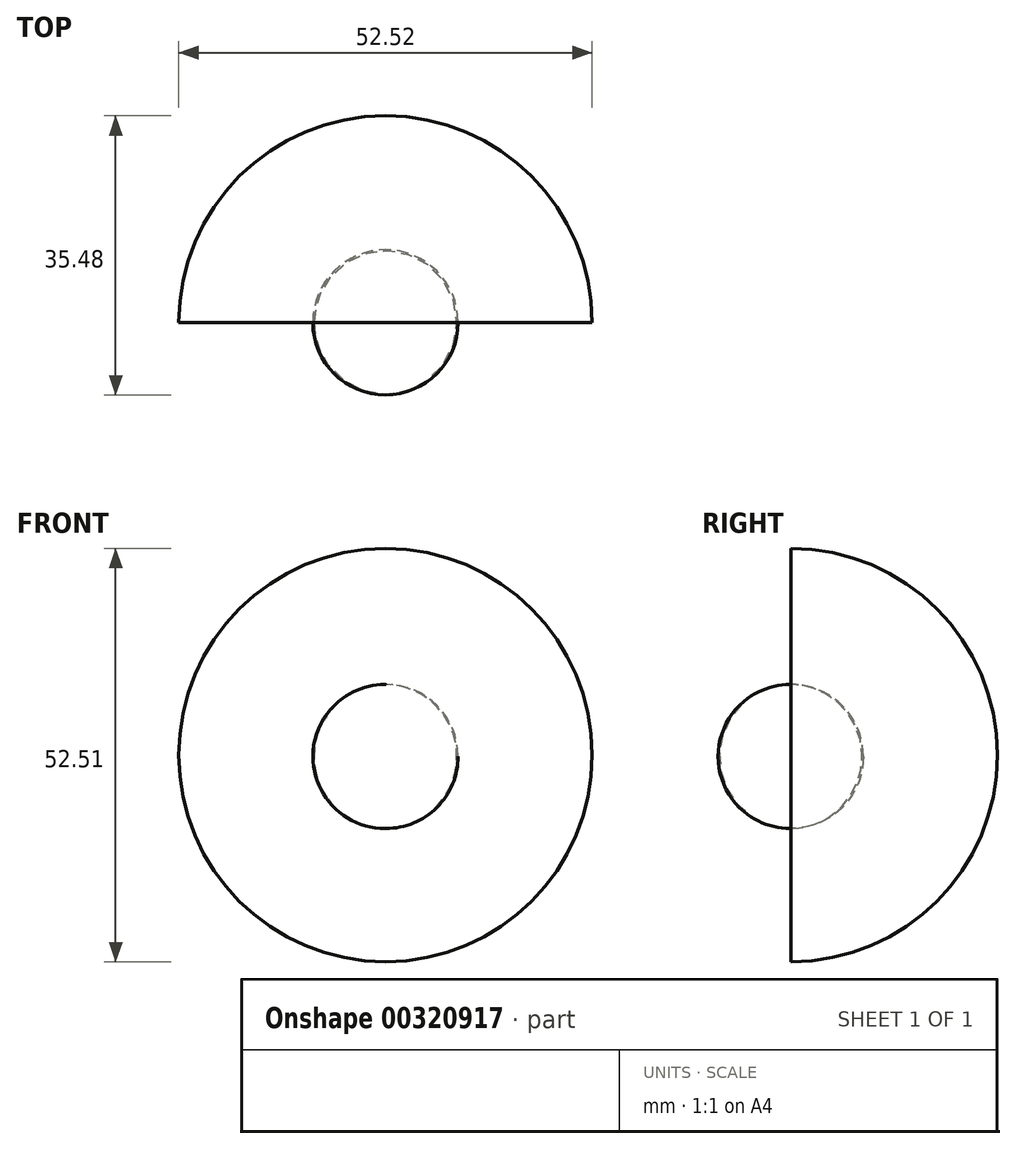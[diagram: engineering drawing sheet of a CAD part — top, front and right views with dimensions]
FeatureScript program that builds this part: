
annotation { "Feature Type Name" : "Feature", "Feature Type Description" : "" }
export const myFeature = defineFeature(function(context is Context, id is Id, definition is map)
    precondition{}
    {
        {
            var Q0;
            Q0=qCreatedBy(makeId("Front.planeOp"),FACE);
            var sketch = newSketch(context, id + "F0", { "sketchPlane" : qUnion([Q0])});
            skLineSegment(sketch, "E0", {"start": v(0, 0) * mm, "end": v(0, 52.51) * mm});
            skArc(sketch, "E1", {"start": v(0, 0) * mm, "mid": v(26.26, 26.26) * mm, "end": v(0, 52.51) * mm});
            skSolve(sketch);
        }
        {
            var Q0;
            Q0=makeQuery(id+"F0.imprint","IMPRINT",FACE,{"disambiguationData":[TD([[makeQuery(id+"F0.imprint","IMPRINT",EDGE,{"derivedFrom":sQuery(id+"F0.wireOp",EDGE,"E0")}),-1.0]])]});
            var Q1;
            Q1=sQuery(id+"F0.wireOp",EDGE,"E0");
            revolve(context, id + "F1", {"entities" : qUnion([Q0]), "axis" : qUnion([Q1]), "revolveType" : RevolveType.ONE_DIRECTION, "angle" : 180 * degree});
        }
        {
            var Q0;
            Q0=makeQuery(id+"F1.opRevolve","CAP_FACE",FACE,{"disambiguationData":[OSD([sQuery(id+"F0.wireOp",EDGE,"E0"),sQuery(id+"F0.wireOp",EDGE,"E1")])],"isStart":true});
            var sketch = newSketch(context, id + "F2", { "sketchPlane" : qUnion([Q0])});
            skLineSegment(sketch, "E2", {"start": v(0, 35.23) * mm, "end": v(0, 16.94) * mm});
            skArc(sketch, "E3", {"start": v(0, 16.94) * mm, "mid": v(9.22, 26.09) * mm, "end": v(0, 35.23) * mm});
            skSolve(sketch);
        }
        {
            var Q0;
            Q0 = qSketchRegion(id + "F2", true);
            var Q1;
            Q1=sQuery(id+"F2.wireOp",EDGE,"E2");
            revolve(context, id + "F3", {"entities" : qUnion([Q0]), "axis" : qUnion([Q1]), "revolveType" : RevolveType.FULL});
        }
    });
